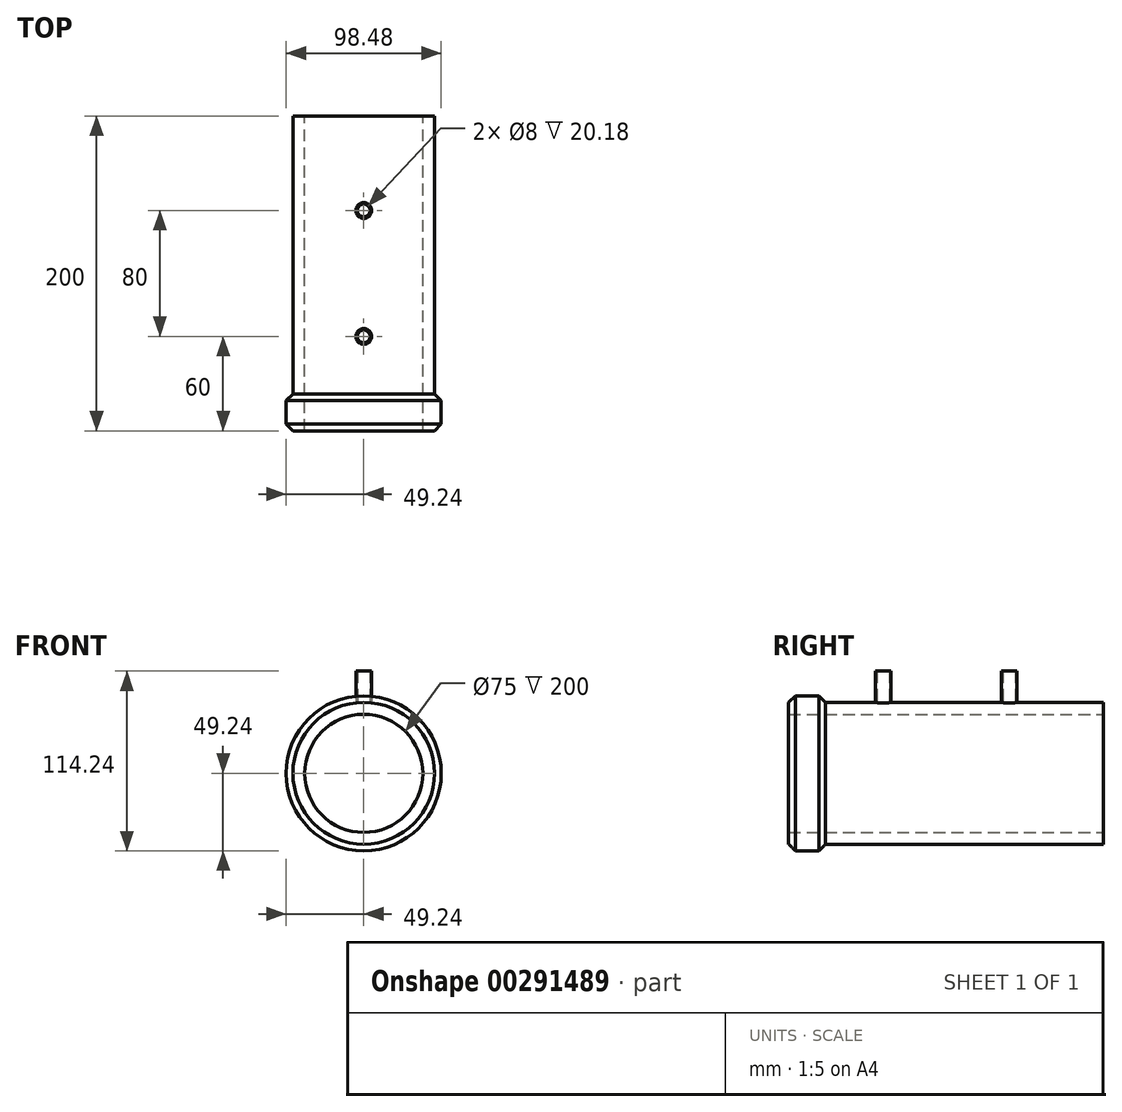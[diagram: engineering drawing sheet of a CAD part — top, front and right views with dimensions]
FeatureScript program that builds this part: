
annotation { "Feature Type Name" : "Feature", "Feature Type Description" : "" }
export const myFeature = defineFeature(function(context is Context, id is Id, definition is map)
    precondition{}
    {
        {
            var Q0;
            Q0=qCreatedBy(makeId("Front.planeOp"),FACE);
            var sketch = newSketch(context, id + "F0", { "sketchPlane" : qUnion([Q0])});
            skCircle(sketch, "E0", {"center": v(0, 0) * mm, "radius": 37.5 * mm});
            skCircle(sketch, "E1", {"center": v(0, 0) * mm, "radius": 45 * mm});
            skSolve(sketch);
        }
        {
            var Q0;
            Q0=makeQuery(id+"F0.imprint","IMPRINT",FACE,{"disambiguationData":[TD([[makeQuery(id+"F0.imprint","IMPRINT",EDGE,{"derivedFrom":sQuery(id+"F0.wireOp",EDGE,"E0")}),-1.0]])]});
            extrude(context, id + "F1", {"entities" : qUnion([Q0]), "endBound" : BoundingType.SYMMETRIC, "depth" : 200 * mm});
        }
        {
            var Q0;
            Q0=qCreatedBy(makeId("Top.planeOp"),FACE);
            cPlane(context, id + "F2", {"entities" : qUnion([Q0]), "cplaneType" : CPlaneType.OFFSET, "offset" : 45 * mm, "width" : 150 * mm, "height" : 150 * mm});
        }
        {
            var Q0;
            Q0=qCreatedBy(id+"F2.planeOp",FACE);
            var sketch = newSketch(context, id + "F3", { "sketchPlane" : qUnion([Q0])});
            skCircle(sketch, "E2", {"center": v(0, 40) * mm, "radius": 5 * mm});
            skCircle(sketch, "E3", {"center": v(0, -40) * mm, "radius": 5 * mm});
            skCircle(sketch, "E4", {"center": v(0, 40) * mm, "radius": 4 * mm});
            skCircle(sketch, "E5", {"center": v(0, -40) * mm, "radius": 4 * mm});
            skSolve(sketch);
        }
        {
            var Q0;
            Q0=makeQuery(id+"F3.imprint","IMPRINT",FACE,{"disambiguationData":[TD([[makeQuery(id+"F3.imprint","IMPRINT",EDGE,{"derivedFrom":sQuery(id+"F3.wireOp",EDGE,"E2")}),1.0]])]});
            var Q1;
            Q1=makeQuery(id+"F3.imprint","IMPRINT",FACE,{"disambiguationData":[TD([[makeQuery(id+"F3.imprint","IMPRINT",EDGE,{"derivedFrom":sQuery(id+"F3.wireOp",EDGE,"E3")}),1.0]])]});
            extrude(context, id + "F4", {"entities" : qUnion([Q0, Q1]), "operationType" : NewBodyOperationType.ADD, "depth" : 20 * mm, "hasSecondDirection" : true, "secondDirectionOppositeDirection" : true, "secondDirectionDepth" : 5 * mm});
        }
        {
            var Q0;
            Q0=qCreatedBy(makeId("Top.planeOp"),FACE);
            var sketch = newSketch(context, id + "F5", { "sketchPlane" : qUnion([Q0])});
            skLineSegment(sketch, "E6", {"start": v(45, 100) * mm, "end": v(45, -100) * mm});
            skLineSegment(sketch, "E7", {"start": v(-45, -100) * mm, "end": v(-45, 100) * mm});
            skLineSegment(sketch, "E8", {"start": v(-45, -100) * mm, "end": v(-49.24, -95.76) * mm});
            skLineSegment(sketch, "E9", {"start": v(-49.24, -95.76) * mm, "end": v(-49.24, -80.76) * mm});
            skLineSegment(sketch, "E10", {"start": v(-49.24, -80.76) * mm, "end": v(-45, -76.51) * mm});
            skLineSegment(sketch, "E11", {"start": v(-45, -100) * mm, "end": v(-45, -76.51) * mm});
            skLineSegment(sketch, "E12", {"start": v(0, -127.53) * mm, "end": v(0, 149.67) * mm, "construction": true});
            skSolve(sketch);
        }
        {
            var Q0;
            Q0=makeQuery(id+"F5.imprint","IMPRINT",FACE,{"disambiguationData":[TD([[makeQuery(id+"F5.imprint","IMPRINT",EDGE,{"derivedFrom":sQuery(id+"F5.wireOp",EDGE,"E8")}),-1.0]])]});
            var Q1;
            Q1=sQuery(id+"F5.wireOp",EDGE,"E12");
            revolve(context, id + "F6", {"operationType" : NewBodyOperationType.ADD, "entities" : qUnion([Q0]), "axis" : qUnion([Q1]), "revolveType" : RevolveType.FULL});
        }
    });
